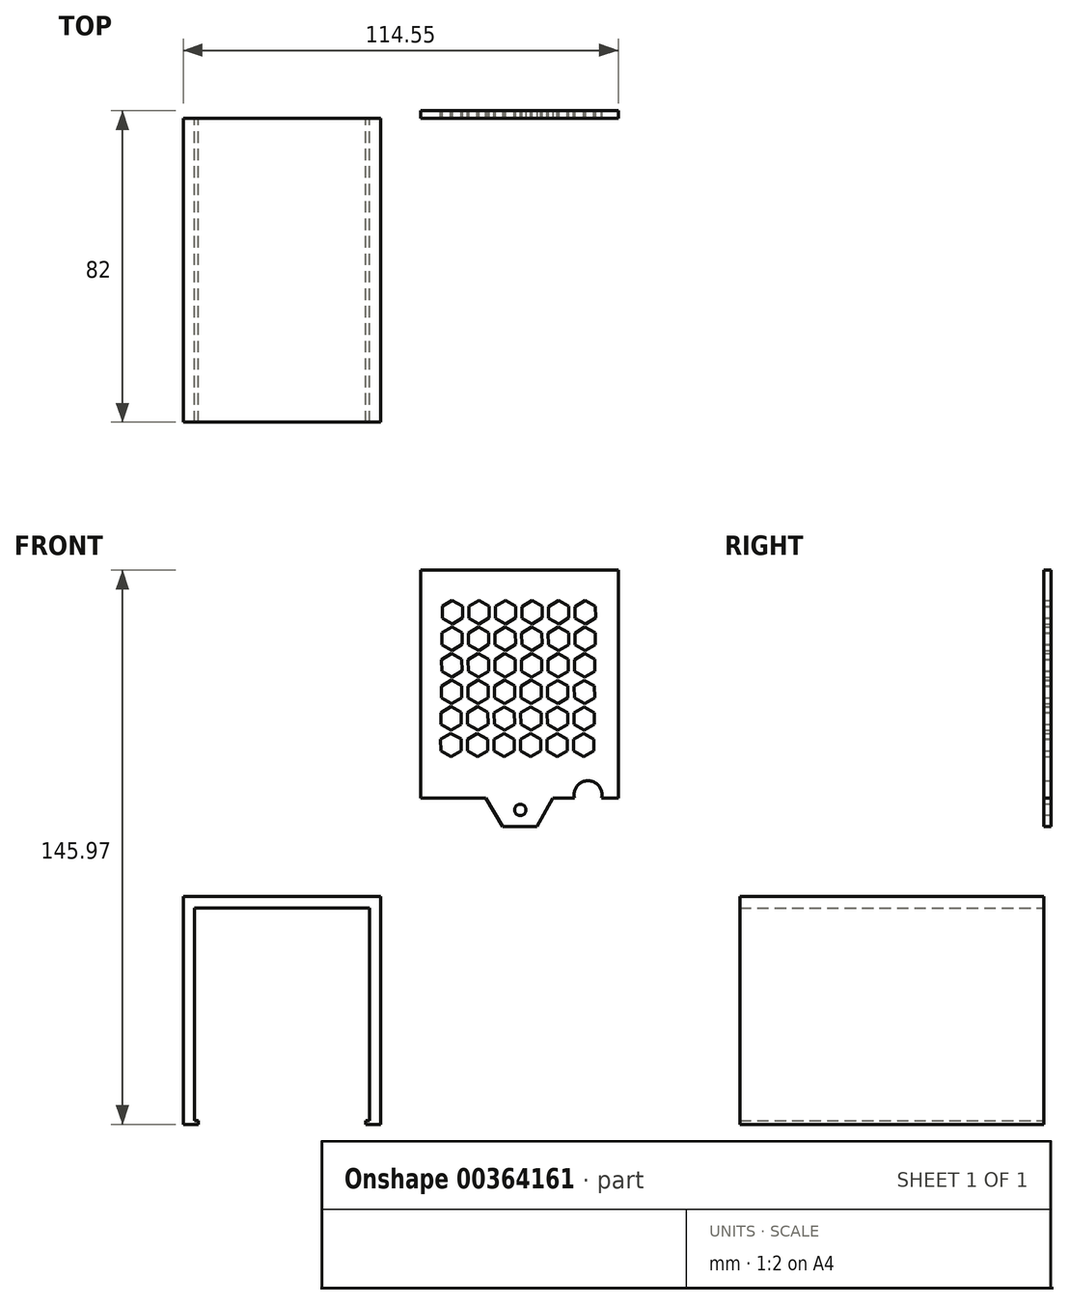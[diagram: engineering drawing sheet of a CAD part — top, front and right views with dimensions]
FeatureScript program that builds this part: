
annotation { "Feature Type Name" : "Feature", "Feature Type Description" : "" }
export const myFeature = defineFeature(function(context is Context, id is Id, definition is map)
    precondition{}
    {
        {
            var Q0;
            Q0=qCreatedBy(makeId("Front.planeOp"),FACE);
            var sketch = newSketch(context, id + "F0", { "sketchPlane" : qUnion([Q0])});
            skLineSegment(sketch, "E0", {"start": v(-25.2, -51.06) * mm, "end": v(-29.2, -51.06) * mm});
            skLineSegment(sketch, "E1", {"start": v(-29.2, -51.06) * mm, "end": v(-29.2, 8.94) * mm});
            skLineSegment(sketch, "E2", {"start": v(-29.2, 8.94) * mm, "end": v(22.8, 8.94) * mm});
            skLineSegment(sketch, "E3", {"start": v(22.8, 8.94) * mm, "end": v(22.8, -51.06) * mm});
            skLineSegment(sketch, "E4", {"start": v(22.8, -51.06) * mm, "end": v(18.8, -51.06) * mm});
            skLineSegment(sketch, "E5", {"start": v(18.8, -51.06) * mm, "end": v(18.8, -50.06) * mm});
            skLineSegment(sketch, "E6", {"start": v(18.8, -50.06) * mm, "end": v(19.8, -50.06) * mm});
            skLineSegment(sketch, "E7", {"start": v(19.8, -50.06) * mm, "end": v(19.8, 5.94) * mm});
            skLineSegment(sketch, "E8", {"start": v(19.8, 5.94) * mm, "end": v(-26.2, 5.94) * mm});
            skLineSegment(sketch, "E9", {"start": v(-26.2, 5.94) * mm, "end": v(-26.2, -50.06) * mm});
            skLineSegment(sketch, "E10", {"start": v(-26.2, -50.06) * mm, "end": v(-25.2, -50.06) * mm});
            skLineSegment(sketch, "E11", {"start": v(-25.2, -50.06) * mm, "end": v(-25.2, -51.06) * mm});
            skSolve(sketch);
        }
        {
            var Q0;
            Q0=makeQuery(id+"F0.imprint","IMPRINT",FACE,{"disambiguationData":[TD([[makeQuery(id+"F0.imprint","IMPRINT",EDGE,{"derivedFrom":sQuery(id+"F0.wireOp",EDGE,"E0")}),-1.0]])]});
            extrude(context, id + "F1", {"entities" : qUnion([Q0]), "depth" : 80 * mm});
        }
        {
            var Q0;
            Q0=qCreatedBy(makeId("Front.planeOp"),FACE);
            var sketch = newSketch(context, id + "F2", { "sketchPlane" : qUnion([Q0])});
            skLineSegment(sketch, "E12.bottom", {"start": v(85.34, 94.91) * mm, "end": v(33.34, 94.91) * mm});
            skLineSegment(sketch, "E12.top", {"start": v(85.34, 34.91) * mm, "end": v(33.34, 34.91) * mm});
            skLineSegment(sketch, "E12.left", {"start": v(85.34, 94.91) * mm, "end": v(85.34, 34.91) * mm});
            skLineSegment(sketch, "E12.right", {"start": v(33.34, 94.91) * mm, "end": v(33.34, 34.91) * mm});
            skSolve(sketch);
        }
        {
            var Q0;
            Q0=makeQuery(id+"F2.imprint","IMPRINT",FACE,{"disambiguationData":[TD([[makeQuery(id+"F2.imprint","IMPRINT",EDGE,{"derivedFrom":sQuery(id+"F2.wireOp",EDGE,"E12.bottom")}),1.0]])]});
            extrude(context, id + "F3", {"entities" : qUnion([Q0]), "oppositeDirection" : true, "depth" : 2 * mm});
        }
        {
            var Q0;
            Q0=makeQuery(id+"F3.opExtrude","CAP_FACE",FACE,{"disambiguationData":[OSD([sQuery(id+"F2.wireOp",EDGE,"E12.bottom"),sQuery(id+"F2.wireOp",EDGE,"E12.top"),sQuery(id+"F2.wireOp",EDGE,"E12.left"),sQuery(id+"F2.wireOp",EDGE,"E12.right")])],"isStart":false});
            var sketch = newSketch(context, id + "F4", { "sketchPlane" : qUnion([Q0])});
            skCircle(sketch, "E13.cCircle", {"center": v(-76.67, 83.82) * mm, "radius": 2.68 * mm, "construction": true});
            skLineSegment(sketch, "E13.0", {"start": v(-74, 82.25) * mm, "end": v(-76.7, 80.74) * mm});
            skLineSegment(sketch, "E13.1", {"start": v(-76.7, 80.74) * mm, "end": v(-79.36, 82.3) * mm});
            skLineSegment(sketch, "E13.2", {"start": v(-79.36, 82.3) * mm, "end": v(-79.33, 85.4) * mm});
            skLineSegment(sketch, "E13.3", {"start": v(-79.33, 85.4) * mm, "end": v(-76.63, 86.91) * mm});
            skLineSegment(sketch, "E13.4", {"start": v(-76.63, 86.91) * mm, "end": v(-73.98, 85.34) * mm});
            skLineSegment(sketch, "E13.5", {"start": v(-73.98, 85.34) * mm, "end": v(-74, 82.25) * mm});
            skPoint(sketch, "E13.0.midPoint", {"position": v(-75.36, 81.5) * mm});
            skLineSegment(sketch, "E14.1.0.0", {"start": v(-72.33, 85.4) * mm, "end": v(-69.63, 86.92) * mm});
            skLineSegment(sketch, "E14.1.0.1", {"start": v(-72.36, 82.32) * mm, "end": v(-72.33, 85.4) * mm});
            skLineSegment(sketch, "E14.1.0.2", {"start": v(-69.7, 80.74) * mm, "end": v(-72.36, 82.32) * mm});
            skLineSegment(sketch, "E14.1.0.3", {"start": v(-67, 82.26) * mm, "end": v(-69.7, 80.74) * mm});
            skPoint(sketch, "E14.1.0.4", {"position": v(-68.36, 81.5) * mm});
            skCircle(sketch, "E14.1.0.5", {"center": v(-69.67, 83.83) * mm, "radius": 2.68 * mm, "construction": true});
            skLineSegment(sketch, "E14.1.0.6", {"start": v(-66.98, 85.34) * mm, "end": v(-67, 82.26) * mm});
            skLineSegment(sketch, "E14.1.0.7", {"start": v(-69.63, 86.92) * mm, "end": v(-66.98, 85.34) * mm});
            skLineSegment(sketch, "E14.2.0.0", {"start": v(-65.33, 85.4) * mm, "end": v(-62.63, 86.92) * mm});
            skLineSegment(sketch, "E14.2.0.1", {"start": v(-65.36, 82.32) * mm, "end": v(-65.33, 85.4) * mm});
            skLineSegment(sketch, "E14.2.0.2", {"start": v(-62.7, 80.75) * mm, "end": v(-65.36, 82.32) * mm});
            skLineSegment(sketch, "E14.2.0.3", {"start": v(-60, 82.26) * mm, "end": v(-62.7, 80.75) * mm});
            skPoint(sketch, "E14.2.0.4", {"position": v(-61.36, 81.5) * mm});
            skCircle(sketch, "E14.2.0.5", {"center": v(-62.67, 83.84) * mm, "radius": 2.68 * mm, "construction": true});
            skLineSegment(sketch, "E14.2.0.6", {"start": v(-59.98, 85.35) * mm, "end": v(-60, 82.26) * mm});
            skLineSegment(sketch, "E14.2.0.7", {"start": v(-62.63, 86.92) * mm, "end": v(-59.98, 85.35) * mm});
            skLineSegment(sketch, "E14.3.0.0", {"start": v(-58.33, 85.42) * mm, "end": v(-55.63, 86.93) * mm});
            skLineSegment(sketch, "E14.3.0.1", {"start": v(-58.36, 82.33) * mm, "end": v(-58.33, 85.42) * mm});
            skLineSegment(sketch, "E14.3.0.2", {"start": v(-55.7, 80.75) * mm, "end": v(-58.36, 82.33) * mm});
            skLineSegment(sketch, "E14.3.0.3", {"start": v(-53, 82.27) * mm, "end": v(-55.7, 80.75) * mm});
            skPoint(sketch, "E14.3.0.4", {"position": v(-54.36, 81.5) * mm});
            skCircle(sketch, "E14.3.0.5", {"center": v(-55.67, 83.84) * mm, "radius": 2.68 * mm, "construction": true});
            skLineSegment(sketch, "E14.3.0.6", {"start": v(-52.98, 85.36) * mm, "end": v(-53, 82.27) * mm});
            skLineSegment(sketch, "E14.3.0.7", {"start": v(-55.63, 86.93) * mm, "end": v(-52.98, 85.36) * mm});
            skLineSegment(sketch, "E14.4.0.0", {"start": v(-51.33, 85.42) * mm, "end": v(-48.63, 86.94) * mm});
            skLineSegment(sketch, "E14.4.0.1", {"start": v(-51.36, 82.33) * mm, "end": v(-51.33, 85.42) * mm});
            skLineSegment(sketch, "E14.4.0.2", {"start": v(-48.7, 80.76) * mm, "end": v(-51.36, 82.33) * mm});
            skLineSegment(sketch, "E14.4.0.3", {"start": v(-46, 82.27) * mm, "end": v(-48.7, 80.76) * mm});
            skPoint(sketch, "E14.4.0.4", {"position": v(-47.36, 81.52) * mm});
            skCircle(sketch, "E14.4.0.5", {"center": v(-48.67, 83.85) * mm, "radius": 2.68 * mm, "construction": true});
            skLineSegment(sketch, "E14.4.0.6", {"start": v(-45.98, 85.36) * mm, "end": v(-46, 82.27) * mm});
            skLineSegment(sketch, "E14.4.0.7", {"start": v(-48.63, 86.94) * mm, "end": v(-45.98, 85.36) * mm});
            skLineSegment(sketch, "E14.5.0.0", {"start": v(-44.33, 85.43) * mm, "end": v(-41.63, 86.94) * mm});
            skLineSegment(sketch, "E14.5.0.1", {"start": v(-44.36, 82.34) * mm, "end": v(-44.33, 85.43) * mm});
            skLineSegment(sketch, "E14.5.0.2", {"start": v(-41.7, 80.76) * mm, "end": v(-44.36, 82.34) * mm});
            skLineSegment(sketch, "E14.5.0.3", {"start": v(-39, 82.28) * mm, "end": v(-41.7, 80.76) * mm});
            skPoint(sketch, "E14.5.0.4", {"position": v(-40.36, 81.52) * mm});
            skCircle(sketch, "E14.5.0.5", {"center": v(-41.67, 83.85) * mm, "radius": 2.68 * mm, "construction": true});
            skLineSegment(sketch, "E14.5.0.6", {"start": v(-38.98, 85.37) * mm, "end": v(-39, 82.28) * mm});
            skLineSegment(sketch, "E14.5.0.7", {"start": v(-41.63, 86.94) * mm, "end": v(-38.98, 85.37) * mm});
            skLineSegment(sketch, "E14.direction1", {"start": v(-79.36, 82.3) * mm, "end": v(-72.36, 82.32) * mm, "construction": true});
            skPoint(sketch, "E15.1.0.0", {"position": v(-75.28, 74.5) * mm});
            skPoint(sketch, "E15.1.0.1", {"position": v(-68.28, 74.5) * mm});
            skPoint(sketch, "E15.1.0.2", {"position": v(-61.28, 74.5) * mm});
            skPoint(sketch, "E15.1.0.3", {"position": v(-54.28, 74.51) * mm});
            skPoint(sketch, "E15.1.0.4", {"position": v(-47.28, 74.52) * mm});
            skPoint(sketch, "E15.1.0.5", {"position": v(-40.28, 74.52) * mm});
            skLineSegment(sketch, "E15.1.0.7", {"start": v(-38.93, 75.28) * mm, "end": v(-41.62, 73.76) * mm});
            skLineSegment(sketch, "E15.1.0.8", {"start": v(-58.28, 75.33) * mm, "end": v(-58.24, 78.42) * mm});
            skLineSegment(sketch, "E15.1.0.9", {"start": v(-55.62, 73.75) * mm, "end": v(-58.28, 75.33) * mm});
            skCircle(sketch, "E15.1.0.10", {"center": v(-41.59, 76.85) * mm, "radius": 2.68 * mm, "construction": true});
            skLineSegment(sketch, "E15.1.0.11", {"start": v(-52.93, 75.27) * mm, "end": v(-55.62, 73.75) * mm});
            skLineSegment(sketch, "E15.1.0.12", {"start": v(-38.9, 78.37) * mm, "end": v(-38.93, 75.28) * mm});
            skCircle(sketch, "E15.1.0.13", {"center": v(-55.59, 76.84) * mm, "radius": 2.68 * mm, "construction": true});
            skLineSegment(sketch, "E15.1.0.14", {"start": v(-52.9, 78.36) * mm, "end": v(-52.93, 75.27) * mm});
            skLineSegment(sketch, "E15.1.0.16", {"start": v(-55.55, 79.93) * mm, "end": v(-52.9, 78.36) * mm});
            skLineSegment(sketch, "E15.1.0.20", {"start": v(-51.28, 75.33) * mm, "end": v(-51.24, 78.42) * mm});
            skLineSegment(sketch, "E15.1.0.22", {"start": v(-48.62, 73.76) * mm, "end": v(-51.28, 75.33) * mm});
            skLineSegment(sketch, "E15.1.0.24", {"start": v(-45.93, 75.27) * mm, "end": v(-48.62, 73.76) * mm});
            skCircle(sketch, "E15.1.0.26", {"center": v(-48.59, 76.85) * mm, "radius": 2.68 * mm, "construction": true});
            skLineSegment(sketch, "E15.1.0.27", {"start": v(-62.62, 73.75) * mm, "end": v(-65.28, 75.32) * mm});
            skLineSegment(sketch, "E15.1.0.28", {"start": v(-79.28, 75.31) * mm, "end": v(-72.28, 75.32) * mm, "construction": true});
            skLineSegment(sketch, "E15.1.0.29", {"start": v(-45.9, 78.36) * mm, "end": v(-45.93, 75.27) * mm});
            skLineSegment(sketch, "E15.1.0.30", {"start": v(-59.93, 75.26) * mm, "end": v(-62.62, 73.75) * mm});
            skLineSegment(sketch, "E15.1.0.31", {"start": v(-48.55, 79.94) * mm, "end": v(-45.9, 78.36) * mm});
            skCircle(sketch, "E15.1.0.32", {"center": v(-62.59, 76.84) * mm, "radius": 2.68 * mm, "construction": true});
            skLineSegment(sketch, "E15.1.0.33", {"start": v(-44.24, 78.43) * mm, "end": v(-41.55, 79.94) * mm});
            skLineSegment(sketch, "E15.1.0.34", {"start": v(-59.9, 78.35) * mm, "end": v(-59.93, 75.26) * mm});
            skLineSegment(sketch, "E15.1.0.35", {"start": v(-69.55, 79.92) * mm, "end": v(-66.9, 78.35) * mm});
            skLineSegment(sketch, "E15.1.0.36", {"start": v(-65.24, 78.41) * mm, "end": v(-62.55, 79.93) * mm});
            skLineSegment(sketch, "E15.1.0.37", {"start": v(-65.28, 75.32) * mm, "end": v(-65.24, 78.41) * mm});
            skCircle(sketch, "E15.1.0.38", {"center": v(-76.59, 76.82) * mm, "radius": 2.68 * mm, "construction": true});
            skLineSegment(sketch, "E15.1.0.39", {"start": v(-73.93, 75.25) * mm, "end": v(-76.62, 73.74) * mm});
            skLineSegment(sketch, "E15.1.0.40", {"start": v(-76.62, 73.74) * mm, "end": v(-79.28, 75.31) * mm});
            skLineSegment(sketch, "E15.1.0.41", {"start": v(-79.28, 75.31) * mm, "end": v(-79.24, 78.4) * mm});
            skLineSegment(sketch, "E15.1.0.42", {"start": v(-76.55, 79.91) * mm, "end": v(-73.9, 78.34) * mm});
            skLineSegment(sketch, "E15.1.0.43", {"start": v(-72.24, 78.4) * mm, "end": v(-69.55, 79.92) * mm});
            skLineSegment(sketch, "E15.1.0.44", {"start": v(-72.28, 75.32) * mm, "end": v(-72.24, 78.4) * mm});
            skLineSegment(sketch, "E15.1.0.45", {"start": v(-69.62, 73.74) * mm, "end": v(-72.28, 75.32) * mm});
            skLineSegment(sketch, "E15.1.0.46", {"start": v(-66.93, 75.26) * mm, "end": v(-69.62, 73.74) * mm});
            skLineSegment(sketch, "E15.1.0.47", {"start": v(-44.28, 75.34) * mm, "end": v(-44.24, 78.43) * mm});
            skLineSegment(sketch, "E15.1.0.48", {"start": v(-62.55, 79.93) * mm, "end": v(-59.9, 78.35) * mm});
            skCircle(sketch, "E15.1.0.49", {"center": v(-69.59, 76.83) * mm, "radius": 2.68 * mm, "construction": true});
            skLineSegment(sketch, "E15.1.0.50", {"start": v(-66.9, 78.35) * mm, "end": v(-66.93, 75.26) * mm});
            skLineSegment(sketch, "E15.1.0.51", {"start": v(-41.62, 73.76) * mm, "end": v(-44.28, 75.34) * mm});
            skLineSegment(sketch, "E15.1.0.52", {"start": v(-58.24, 78.42) * mm, "end": v(-55.55, 79.93) * mm});
            skLineSegment(sketch, "E15.1.0.53", {"start": v(-41.55, 79.94) * mm, "end": v(-38.9, 78.37) * mm});
            skLineSegment(sketch, "E15.1.0.54", {"start": v(-51.24, 78.42) * mm, "end": v(-48.55, 79.94) * mm});
            skLineSegment(sketch, "E15.1.0.55", {"start": v(-79.24, 78.4) * mm, "end": v(-76.55, 79.91) * mm});
            skLineSegment(sketch, "E15.1.0.56", {"start": v(-73.9, 78.34) * mm, "end": v(-73.93, 75.25) * mm});
            skPoint(sketch, "E15.2.0.0", {"position": v(-75.2, 67.5) * mm});
            skPoint(sketch, "E15.2.0.1", {"position": v(-68.2, 67.5) * mm});
            skPoint(sketch, "E15.2.0.2", {"position": v(-61.2, 67.5) * mm});
            skPoint(sketch, "E15.2.0.3", {"position": v(-54.2, 67.51) * mm});
            skPoint(sketch, "E15.2.0.4", {"position": v(-47.2, 67.52) * mm});
            skPoint(sketch, "E15.2.0.5", {"position": v(-40.2, 67.52) * mm});
            skLineSegment(sketch, "E15.2.0.7", {"start": v(-38.85, 68.28) * mm, "end": v(-41.54, 66.76) * mm});
            skLineSegment(sketch, "E15.2.0.8", {"start": v(-58.2, 68.33) * mm, "end": v(-58.16, 71.42) * mm});
            skLineSegment(sketch, "E15.2.0.9", {"start": v(-55.54, 66.75) * mm, "end": v(-58.2, 68.33) * mm});
            skCircle(sketch, "E15.2.0.10", {"center": v(-41.5, 69.85) * mm, "radius": 2.68 * mm, "construction": true});
            skLineSegment(sketch, "E15.2.0.11", {"start": v(-52.85, 68.27) * mm, "end": v(-55.54, 66.75) * mm});
            skLineSegment(sketch, "E15.2.0.12", {"start": v(-38.81, 71.37) * mm, "end": v(-38.85, 68.28) * mm});
            skCircle(sketch, "E15.2.0.13", {"center": v(-55.5, 69.84) * mm, "radius": 2.68 * mm, "construction": true});
            skLineSegment(sketch, "E15.2.0.14", {"start": v(-52.81, 71.36) * mm, "end": v(-52.85, 68.27) * mm});
            skLineSegment(sketch, "E15.2.0.16", {"start": v(-55.47, 72.93) * mm, "end": v(-52.81, 71.36) * mm});
            skLineSegment(sketch, "E15.2.0.20", {"start": v(-51.2, 68.33) * mm, "end": v(-51.16, 71.42) * mm});
            skLineSegment(sketch, "E15.2.0.22", {"start": v(-48.54, 66.76) * mm, "end": v(-51.2, 68.33) * mm});
            skLineSegment(sketch, "E15.2.0.24", {"start": v(-45.85, 68.27) * mm, "end": v(-48.54, 66.76) * mm});
            skCircle(sketch, "E15.2.0.26", {"center": v(-48.5, 69.85) * mm, "radius": 2.68 * mm, "construction": true});
            skLineSegment(sketch, "E15.2.0.27", {"start": v(-62.54, 66.75) * mm, "end": v(-65.2, 68.32) * mm});
            skLineSegment(sketch, "E15.2.0.28", {"start": v(-79.2, 68.31) * mm, "end": v(-72.2, 68.32) * mm, "construction": true});
            skLineSegment(sketch, "E15.2.0.29", {"start": v(-45.81, 71.36) * mm, "end": v(-45.85, 68.27) * mm});
            skLineSegment(sketch, "E15.2.0.30", {"start": v(-59.85, 68.26) * mm, "end": v(-62.54, 66.75) * mm});
            skLineSegment(sketch, "E15.2.0.31", {"start": v(-48.47, 72.94) * mm, "end": v(-45.81, 71.36) * mm});
            skCircle(sketch, "E15.2.0.32", {"center": v(-62.5, 69.84) * mm, "radius": 2.68 * mm, "construction": true});
            skLineSegment(sketch, "E15.2.0.33", {"start": v(-44.16, 71.43) * mm, "end": v(-41.47, 72.94) * mm});
            skLineSegment(sketch, "E15.2.0.34", {"start": v(-59.81, 71.35) * mm, "end": v(-59.85, 68.26) * mm});
            skLineSegment(sketch, "E15.2.0.35", {"start": v(-69.47, 72.92) * mm, "end": v(-66.81, 71.35) * mm});
            skLineSegment(sketch, "E15.2.0.36", {"start": v(-65.16, 71.41) * mm, "end": v(-62.47, 72.93) * mm});
            skLineSegment(sketch, "E15.2.0.37", {"start": v(-65.2, 68.32) * mm, "end": v(-65.16, 71.41) * mm});
            skCircle(sketch, "E15.2.0.38", {"center": v(-76.5, 69.83) * mm, "radius": 2.68 * mm, "construction": true});
            skLineSegment(sketch, "E15.2.0.39", {"start": v(-73.85, 68.25) * mm, "end": v(-76.54, 66.74) * mm});
            skLineSegment(sketch, "E15.2.0.40", {"start": v(-76.54, 66.74) * mm, "end": v(-79.2, 68.31) * mm});
            skLineSegment(sketch, "E15.2.0.41", {"start": v(-79.2, 68.31) * mm, "end": v(-79.16, 71.4) * mm});
            skLineSegment(sketch, "E15.2.0.42", {"start": v(-76.47, 72.91) * mm, "end": v(-73.81, 71.34) * mm});
            skLineSegment(sketch, "E15.2.0.43", {"start": v(-72.16, 71.4) * mm, "end": v(-69.47, 72.92) * mm});
            skLineSegment(sketch, "E15.2.0.44", {"start": v(-72.2, 68.32) * mm, "end": v(-72.16, 71.4) * mm});
            skLineSegment(sketch, "E15.2.0.45", {"start": v(-69.54, 66.74) * mm, "end": v(-72.2, 68.32) * mm});
            skLineSegment(sketch, "E15.2.0.46", {"start": v(-66.85, 68.26) * mm, "end": v(-69.54, 66.74) * mm});
            skLineSegment(sketch, "E15.2.0.47", {"start": v(-44.2, 68.34) * mm, "end": v(-44.16, 71.43) * mm});
            skLineSegment(sketch, "E15.2.0.48", {"start": v(-62.47, 72.93) * mm, "end": v(-59.81, 71.35) * mm});
            skCircle(sketch, "E15.2.0.49", {"center": v(-69.5, 69.83) * mm, "radius": 2.68 * mm, "construction": true});
            skLineSegment(sketch, "E15.2.0.50", {"start": v(-66.81, 71.35) * mm, "end": v(-66.85, 68.26) * mm});
            skLineSegment(sketch, "E15.2.0.51", {"start": v(-41.54, 66.76) * mm, "end": v(-44.2, 68.34) * mm});
            skLineSegment(sketch, "E15.2.0.52", {"start": v(-58.16, 71.42) * mm, "end": v(-55.47, 72.93) * mm});
            skLineSegment(sketch, "E15.2.0.53", {"start": v(-41.47, 72.94) * mm, "end": v(-38.81, 71.37) * mm});
            skLineSegment(sketch, "E15.2.0.54", {"start": v(-51.16, 71.42) * mm, "end": v(-48.47, 72.94) * mm});
            skLineSegment(sketch, "E15.2.0.55", {"start": v(-79.16, 71.4) * mm, "end": v(-76.47, 72.91) * mm});
            skLineSegment(sketch, "E15.2.0.56", {"start": v(-73.81, 71.34) * mm, "end": v(-73.85, 68.25) * mm});
            skPoint(sketch, "E15.3.0.0", {"position": v(-75.11, 60.5) * mm});
            skPoint(sketch, "E15.3.0.1", {"position": v(-68.11, 60.5) * mm});
            skPoint(sketch, "E15.3.0.2", {"position": v(-61.11, 60.5) * mm});
            skPoint(sketch, "E15.3.0.3", {"position": v(-54.11, 60.51) * mm});
            skPoint(sketch, "E15.3.0.4", {"position": v(-47.11, 60.52) * mm});
            skPoint(sketch, "E15.3.0.5", {"position": v(-40.11, 60.52) * mm});
            skLineSegment(sketch, "E15.3.0.7", {"start": v(-38.77, 61.28) * mm, "end": v(-41.46, 59.77) * mm});
            skLineSegment(sketch, "E15.3.0.8", {"start": v(-58.12, 61.33) * mm, "end": v(-58.08, 64.42) * mm});
            skLineSegment(sketch, "E15.3.0.9", {"start": v(-55.46, 59.75) * mm, "end": v(-58.12, 61.33) * mm});
            skCircle(sketch, "E15.3.0.10", {"center": v(-41.43, 62.85) * mm, "radius": 2.68 * mm, "construction": true});
            skLineSegment(sketch, "E15.3.0.11", {"start": v(-52.77, 61.27) * mm, "end": v(-55.46, 59.75) * mm});
            skLineSegment(sketch, "E15.3.0.12", {"start": v(-38.73, 64.37) * mm, "end": v(-38.77, 61.28) * mm});
            skCircle(sketch, "E15.3.0.13", {"center": v(-55.43, 62.84) * mm, "radius": 2.68 * mm, "construction": true});
            skLineSegment(sketch, "E15.3.0.14", {"start": v(-52.73, 64.36) * mm, "end": v(-52.77, 61.27) * mm});
            skLineSegment(sketch, "E15.3.0.16", {"start": v(-55.4, 65.93) * mm, "end": v(-52.73, 64.36) * mm});
            skLineSegment(sketch, "E15.3.0.20", {"start": v(-51.12, 61.33) * mm, "end": v(-51.08, 64.42) * mm});
            skLineSegment(sketch, "E15.3.0.22", {"start": v(-48.46, 59.76) * mm, "end": v(-51.12, 61.33) * mm});
            skLineSegment(sketch, "E15.3.0.24", {"start": v(-45.77, 61.27) * mm, "end": v(-48.46, 59.76) * mm});
            skCircle(sketch, "E15.3.0.26", {"center": v(-48.43, 62.85) * mm, "radius": 2.68 * mm, "construction": true});
            skLineSegment(sketch, "E15.3.0.27", {"start": v(-62.46, 59.75) * mm, "end": v(-65.12, 61.32) * mm});
            skLineSegment(sketch, "E15.3.0.28", {"start": v(-79.12, 61.31) * mm, "end": v(-72.12, 61.32) * mm, "construction": true});
            skLineSegment(sketch, "E15.3.0.29", {"start": v(-45.73, 64.36) * mm, "end": v(-45.77, 61.27) * mm});
            skLineSegment(sketch, "E15.3.0.30", {"start": v(-59.77, 61.26) * mm, "end": v(-62.46, 59.75) * mm});
            skLineSegment(sketch, "E15.3.0.31", {"start": v(-48.4, 65.94) * mm, "end": v(-45.73, 64.36) * mm});
            skCircle(sketch, "E15.3.0.32", {"center": v(-62.43, 62.84) * mm, "radius": 2.68 * mm, "construction": true});
            skLineSegment(sketch, "E15.3.0.33", {"start": v(-44.08, 64.43) * mm, "end": v(-41.4, 65.94) * mm});
            skLineSegment(sketch, "E15.3.0.34", {"start": v(-59.73, 64.35) * mm, "end": v(-59.77, 61.26) * mm});
            skLineSegment(sketch, "E15.3.0.35", {"start": v(-69.4, 65.92) * mm, "end": v(-66.73, 64.35) * mm});
            skLineSegment(sketch, "E15.3.0.36", {"start": v(-65.08, 64.41) * mm, "end": v(-62.4, 65.93) * mm});
            skLineSegment(sketch, "E15.3.0.37", {"start": v(-65.12, 61.32) * mm, "end": v(-65.08, 64.41) * mm});
            skCircle(sketch, "E15.3.0.38", {"center": v(-76.43, 62.83) * mm, "radius": 2.68 * mm, "construction": true});
            skLineSegment(sketch, "E15.3.0.39", {"start": v(-73.77, 61.25) * mm, "end": v(-76.46, 59.74) * mm});
            skLineSegment(sketch, "E15.3.0.40", {"start": v(-76.46, 59.74) * mm, "end": v(-79.12, 61.31) * mm});
            skLineSegment(sketch, "E15.3.0.41", {"start": v(-79.12, 61.31) * mm, "end": v(-79.08, 64.4) * mm});
            skLineSegment(sketch, "E15.3.0.42", {"start": v(-76.4, 65.91) * mm, "end": v(-73.73, 64.34) * mm});
            skLineSegment(sketch, "E15.3.0.43", {"start": v(-72.08, 64.4) * mm, "end": v(-69.4, 65.92) * mm});
            skLineSegment(sketch, "E15.3.0.44", {"start": v(-72.12, 61.32) * mm, "end": v(-72.08, 64.4) * mm});
            skLineSegment(sketch, "E15.3.0.45", {"start": v(-69.46, 59.74) * mm, "end": v(-72.12, 61.32) * mm});
            skLineSegment(sketch, "E15.3.0.46", {"start": v(-66.77, 61.26) * mm, "end": v(-69.46, 59.74) * mm});
            skLineSegment(sketch, "E15.3.0.47", {"start": v(-44.12, 61.34) * mm, "end": v(-44.08, 64.43) * mm});
            skLineSegment(sketch, "E15.3.0.48", {"start": v(-62.4, 65.93) * mm, "end": v(-59.73, 64.35) * mm});
            skCircle(sketch, "E15.3.0.49", {"center": v(-69.43, 62.83) * mm, "radius": 2.68 * mm, "construction": true});
            skLineSegment(sketch, "E15.3.0.50", {"start": v(-66.73, 64.35) * mm, "end": v(-66.77, 61.26) * mm});
            skLineSegment(sketch, "E15.3.0.51", {"start": v(-41.46, 59.77) * mm, "end": v(-44.12, 61.34) * mm});
            skLineSegment(sketch, "E15.3.0.52", {"start": v(-58.08, 64.42) * mm, "end": v(-55.4, 65.93) * mm});
            skLineSegment(sketch, "E15.3.0.53", {"start": v(-41.4, 65.94) * mm, "end": v(-38.73, 64.37) * mm});
            skLineSegment(sketch, "E15.3.0.54", {"start": v(-51.08, 64.42) * mm, "end": v(-48.4, 65.94) * mm});
            skLineSegment(sketch, "E15.3.0.55", {"start": v(-79.08, 64.4) * mm, "end": v(-76.4, 65.91) * mm});
            skLineSegment(sketch, "E15.3.0.56", {"start": v(-73.73, 64.34) * mm, "end": v(-73.77, 61.25) * mm});
            skPoint(sketch, "E15.4.0.0", {"position": v(-75.03, 53.5) * mm});
            skPoint(sketch, "E15.4.0.1", {"position": v(-68.03, 53.5) * mm});
            skPoint(sketch, "E15.4.0.2", {"position": v(-61.03, 53.5) * mm});
            skPoint(sketch, "E15.4.0.3", {"position": v(-54.03, 53.51) * mm});
            skPoint(sketch, "E15.4.0.4", {"position": v(-47.03, 53.52) * mm});
            skPoint(sketch, "E15.4.0.5", {"position": v(-40.03, 53.52) * mm});
            skLineSegment(sketch, "E15.4.0.7", {"start": v(-38.69, 54.28) * mm, "end": v(-41.38, 52.77) * mm});
            skLineSegment(sketch, "E15.4.0.8", {"start": v(-58.04, 54.33) * mm, "end": v(-58, 57.42) * mm});
            skLineSegment(sketch, "E15.4.0.9", {"start": v(-55.38, 52.75) * mm, "end": v(-58.04, 54.33) * mm});
            skCircle(sketch, "E15.4.0.10", {"center": v(-41.34, 55.85) * mm, "radius": 2.68 * mm, "construction": true});
            skLineSegment(sketch, "E15.4.0.11", {"start": v(-52.69, 54.27) * mm, "end": v(-55.38, 52.75) * mm});
            skLineSegment(sketch, "E15.4.0.12", {"start": v(-38.65, 57.37) * mm, "end": v(-38.69, 54.28) * mm});
            skCircle(sketch, "E15.4.0.13", {"center": v(-55.34, 55.84) * mm, "radius": 2.68 * mm, "construction": true});
            skLineSegment(sketch, "E15.4.0.14", {"start": v(-52.65, 57.36) * mm, "end": v(-52.69, 54.27) * mm});
            skLineSegment(sketch, "E15.4.0.16", {"start": v(-55.31, 58.93) * mm, "end": v(-52.65, 57.36) * mm});
            skLineSegment(sketch, "E15.4.0.20", {"start": v(-51.04, 54.33) * mm, "end": v(-51, 57.42) * mm});
            skLineSegment(sketch, "E15.4.0.22", {"start": v(-48.38, 52.76) * mm, "end": v(-51.04, 54.33) * mm});
            skLineSegment(sketch, "E15.4.0.24", {"start": v(-45.69, 54.27) * mm, "end": v(-48.38, 52.76) * mm});
            skCircle(sketch, "E15.4.0.26", {"center": v(-48.34, 55.85) * mm, "radius": 2.68 * mm, "construction": true});
            skLineSegment(sketch, "E15.4.0.27", {"start": v(-62.38, 52.75) * mm, "end": v(-65.04, 54.32) * mm});
            skLineSegment(sketch, "E15.4.0.28", {"start": v(-79.04, 54.31) * mm, "end": v(-72.04, 54.32) * mm, "construction": true});
            skLineSegment(sketch, "E15.4.0.29", {"start": v(-45.65, 57.36) * mm, "end": v(-45.69, 54.27) * mm});
            skLineSegment(sketch, "E15.4.0.30", {"start": v(-59.69, 54.26) * mm, "end": v(-62.38, 52.75) * mm});
            skLineSegment(sketch, "E15.4.0.31", {"start": v(-48.31, 58.94) * mm, "end": v(-45.65, 57.36) * mm});
            skCircle(sketch, "E15.4.0.32", {"center": v(-62.34, 55.84) * mm, "radius": 2.68 * mm, "construction": true});
            skLineSegment(sketch, "E15.4.0.33", {"start": v(-44, 57.43) * mm, "end": v(-41.31, 58.94) * mm});
            skLineSegment(sketch, "E15.4.0.34", {"start": v(-59.65, 57.35) * mm, "end": v(-59.69, 54.26) * mm});
            skLineSegment(sketch, "E15.4.0.35", {"start": v(-69.31, 58.92) * mm, "end": v(-66.65, 57.35) * mm});
            skLineSegment(sketch, "E15.4.0.36", {"start": v(-65, 57.41) * mm, "end": v(-62.31, 58.93) * mm});
            skLineSegment(sketch, "E15.4.0.37", {"start": v(-65.04, 54.32) * mm, "end": v(-65, 57.41) * mm});
            skCircle(sketch, "E15.4.0.38", {"center": v(-76.34, 55.83) * mm, "radius": 2.68 * mm, "construction": true});
            skLineSegment(sketch, "E15.4.0.39", {"start": v(-73.69, 54.25) * mm, "end": v(-76.38, 52.74) * mm});
            skLineSegment(sketch, "E15.4.0.40", {"start": v(-76.38, 52.74) * mm, "end": v(-79.04, 54.31) * mm});
            skLineSegment(sketch, "E15.4.0.41", {"start": v(-79.04, 54.31) * mm, "end": v(-79, 57.4) * mm});
            skLineSegment(sketch, "E15.4.0.42", {"start": v(-76.31, 58.92) * mm, "end": v(-73.65, 57.34) * mm});
            skLineSegment(sketch, "E15.4.0.43", {"start": v(-72, 57.4) * mm, "end": v(-69.31, 58.92) * mm});
            skLineSegment(sketch, "E15.4.0.44", {"start": v(-72.04, 54.32) * mm, "end": v(-72, 57.4) * mm});
            skLineSegment(sketch, "E15.4.0.45", {"start": v(-69.38, 52.74) * mm, "end": v(-72.04, 54.32) * mm});
            skLineSegment(sketch, "E15.4.0.46", {"start": v(-66.69, 54.26) * mm, "end": v(-69.38, 52.74) * mm});
            skLineSegment(sketch, "E15.4.0.47", {"start": v(-44.04, 54.34) * mm, "end": v(-44, 57.43) * mm});
            skLineSegment(sketch, "E15.4.0.48", {"start": v(-62.31, 58.93) * mm, "end": v(-59.65, 57.35) * mm});
            skCircle(sketch, "E15.4.0.49", {"center": v(-69.34, 55.83) * mm, "radius": 2.68 * mm, "construction": true});
            skLineSegment(sketch, "E15.4.0.50", {"start": v(-66.65, 57.35) * mm, "end": v(-66.69, 54.26) * mm});
            skLineSegment(sketch, "E15.4.0.51", {"start": v(-41.38, 52.77) * mm, "end": v(-44.04, 54.34) * mm});
            skLineSegment(sketch, "E15.4.0.52", {"start": v(-58, 57.42) * mm, "end": v(-55.31, 58.93) * mm});
            skLineSegment(sketch, "E15.4.0.53", {"start": v(-41.31, 58.94) * mm, "end": v(-38.65, 57.37) * mm});
            skLineSegment(sketch, "E15.4.0.54", {"start": v(-51, 57.42) * mm, "end": v(-48.31, 58.94) * mm});
            skLineSegment(sketch, "E15.4.0.55", {"start": v(-79, 57.4) * mm, "end": v(-76.31, 58.92) * mm});
            skLineSegment(sketch, "E15.4.0.56", {"start": v(-73.65, 57.34) * mm, "end": v(-73.69, 54.25) * mm});
            skPoint(sketch, "E15.5.0.0", {"position": v(-74.95, 46.5) * mm});
            skPoint(sketch, "E15.5.0.1", {"position": v(-67.95, 46.5) * mm});
            skPoint(sketch, "E15.5.0.2", {"position": v(-60.95, 46.5) * mm});
            skPoint(sketch, "E15.5.0.3", {"position": v(-53.95, 46.51) * mm});
            skPoint(sketch, "E15.5.0.4", {"position": v(-46.95, 46.52) * mm});
            skPoint(sketch, "E15.5.0.5", {"position": v(-39.95, 46.52) * mm});
            skLineSegment(sketch, "E15.5.0.7", {"start": v(-38.6, 47.28) * mm, "end": v(-41.3, 45.77) * mm});
            skLineSegment(sketch, "E15.5.0.8", {"start": v(-57.96, 47.33) * mm, "end": v(-57.92, 50.42) * mm});
            skLineSegment(sketch, "E15.5.0.9", {"start": v(-55.3, 45.75) * mm, "end": v(-57.96, 47.33) * mm});
            skCircle(sketch, "E15.5.0.10", {"center": v(-41.26, 48.86) * mm, "radius": 2.68 * mm, "construction": true});
            skLineSegment(sketch, "E15.5.0.11", {"start": v(-52.6, 47.27) * mm, "end": v(-55.3, 45.75) * mm});
            skLineSegment(sketch, "E15.5.0.12", {"start": v(-38.57, 50.37) * mm, "end": v(-38.6, 47.28) * mm});
            skCircle(sketch, "E15.5.0.13", {"center": v(-55.26, 48.84) * mm, "radius": 2.68 * mm, "construction": true});
            skLineSegment(sketch, "E15.5.0.14", {"start": v(-52.57, 50.36) * mm, "end": v(-52.6, 47.27) * mm});
            skLineSegment(sketch, "E15.5.0.16", {"start": v(-55.23, 51.93) * mm, "end": v(-52.57, 50.36) * mm});
            skLineSegment(sketch, "E15.5.0.20", {"start": v(-50.96, 47.33) * mm, "end": v(-50.92, 50.42) * mm});
            skLineSegment(sketch, "E15.5.0.22", {"start": v(-48.3, 45.76) * mm, "end": v(-50.96, 47.33) * mm});
            skLineSegment(sketch, "E15.5.0.24", {"start": v(-45.6, 47.28) * mm, "end": v(-48.3, 45.76) * mm});
            skCircle(sketch, "E15.5.0.26", {"center": v(-48.26, 48.85) * mm, "radius": 2.68 * mm, "construction": true});
            skLineSegment(sketch, "E15.5.0.27", {"start": v(-62.3, 45.75) * mm, "end": v(-64.96, 47.32) * mm});
            skLineSegment(sketch, "E15.5.0.28", {"start": v(-78.96, 47.31) * mm, "end": v(-71.96, 47.32) * mm, "construction": true});
            skLineSegment(sketch, "E15.5.0.29", {"start": v(-45.57, 50.36) * mm, "end": v(-45.6, 47.28) * mm});
            skLineSegment(sketch, "E15.5.0.30", {"start": v(-59.6, 47.26) * mm, "end": v(-62.3, 45.75) * mm});
            skLineSegment(sketch, "E15.5.0.31", {"start": v(-48.23, 51.94) * mm, "end": v(-45.57, 50.36) * mm});
            skCircle(sketch, "E15.5.0.32", {"center": v(-62.26, 48.84) * mm, "radius": 2.68 * mm, "construction": true});
            skLineSegment(sketch, "E15.5.0.33", {"start": v(-43.92, 50.43) * mm, "end": v(-41.23, 51.94) * mm});
            skLineSegment(sketch, "E15.5.0.34", {"start": v(-59.57, 50.35) * mm, "end": v(-59.6, 47.26) * mm});
            skLineSegment(sketch, "E15.5.0.35", {"start": v(-69.23, 51.92) * mm, "end": v(-66.57, 50.35) * mm});
            skLineSegment(sketch, "E15.5.0.36", {"start": v(-64.92, 50.41) * mm, "end": v(-62.23, 51.93) * mm});
            skLineSegment(sketch, "E15.5.0.37", {"start": v(-64.96, 47.32) * mm, "end": v(-64.92, 50.41) * mm});
            skCircle(sketch, "E15.5.0.38", {"center": v(-76.26, 48.83) * mm, "radius": 2.68 * mm, "construction": true});
            skLineSegment(sketch, "E15.5.0.39", {"start": v(-73.6, 47.25) * mm, "end": v(-76.3, 45.74) * mm});
            skLineSegment(sketch, "E15.5.0.40", {"start": v(-76.3, 45.74) * mm, "end": v(-78.96, 47.31) * mm});
            skLineSegment(sketch, "E15.5.0.41", {"start": v(-78.96, 47.31) * mm, "end": v(-78.92, 50.4) * mm});
            skLineSegment(sketch, "E15.5.0.42", {"start": v(-76.23, 51.92) * mm, "end": v(-73.57, 50.34) * mm});
            skLineSegment(sketch, "E15.5.0.43", {"start": v(-71.92, 50.4) * mm, "end": v(-69.23, 51.92) * mm});
            skLineSegment(sketch, "E15.5.0.44", {"start": v(-71.96, 47.32) * mm, "end": v(-71.92, 50.4) * mm});
            skLineSegment(sketch, "E15.5.0.45", {"start": v(-69.3, 45.74) * mm, "end": v(-71.96, 47.32) * mm});
            skLineSegment(sketch, "E15.5.0.46", {"start": v(-66.6, 47.26) * mm, "end": v(-69.3, 45.74) * mm});
            skLineSegment(sketch, "E15.5.0.47", {"start": v(-43.96, 47.34) * mm, "end": v(-43.92, 50.43) * mm});
            skLineSegment(sketch, "E15.5.0.48", {"start": v(-62.23, 51.93) * mm, "end": v(-59.57, 50.35) * mm});
            skCircle(sketch, "E15.5.0.49", {"center": v(-69.26, 48.83) * mm, "radius": 2.68 * mm, "construction": true});
            skLineSegment(sketch, "E15.5.0.50", {"start": v(-66.57, 50.35) * mm, "end": v(-66.6, 47.26) * mm});
            skLineSegment(sketch, "E15.5.0.51", {"start": v(-41.3, 45.77) * mm, "end": v(-43.96, 47.34) * mm});
            skLineSegment(sketch, "E15.5.0.52", {"start": v(-57.92, 50.42) * mm, "end": v(-55.23, 51.93) * mm});
            skLineSegment(sketch, "E15.5.0.53", {"start": v(-41.23, 51.94) * mm, "end": v(-38.57, 50.37) * mm});
            skLineSegment(sketch, "E15.5.0.54", {"start": v(-50.92, 50.42) * mm, "end": v(-48.23, 51.94) * mm});
            skLineSegment(sketch, "E15.5.0.55", {"start": v(-78.92, 50.4) * mm, "end": v(-76.23, 51.92) * mm});
            skLineSegment(sketch, "E15.5.0.56", {"start": v(-73.57, 50.34) * mm, "end": v(-73.6, 47.25) * mm});
            skLineSegment(sketch, "E15.direction1", {"start": v(-79.36, 82.3) * mm, "end": v(-79.28, 75.31) * mm, "construction": true});
            skSolve(sketch);
        }
        {
            var Q0;
            Q0 = qSketchRegion(id + "F4", true);
            extrude(context, id + "F5", {"entities" : qUnion([Q0]), "operationType" : NewBodyOperationType.REMOVE, "oppositeDirection" : true, "depth" : 2 * mm});
        }
        {
            var Q0;
            Q0=qCreatedBy(makeId("Front.planeOp"),FACE);
            var sketch = newSketch(context, id + "F6", { "sketchPlane" : qUnion([Q0])});
            skLineSegment(sketch, "E16.0", {"start": v(63.93, 27.37) * mm, "end": v(54.87, 27.37) * mm});
            skLineSegment(sketch, "E16.1", {"start": v(54.87, 27.37) * mm, "end": v(50.35, 35.21) * mm});
            skLineSegment(sketch, "E16.5", {"start": v(68.35, 35.21) * mm, "end": v(63.93, 27.37) * mm});
            skLineSegment(sketch, "E17", {"start": v(68.35, 35.21) * mm, "end": v(50.35, 35.21) * mm});
            skCircle(sketch, "E18", {"center": v(59.54, 31.74) * mm, "radius": 1.5 * mm});
            skSolve(sketch);
        }
        {
            var Q0;
            Q0=makeQuery(id+"F6.imprint","IMPRINT",FACE,{"disambiguationData":[TD([[makeQuery(id+"F6.imprint","IMPRINT",EDGE,{"derivedFrom":sQuery(id+"F6.wireOp",EDGE,"E16.0")}),-1.0]])]});
            extrude(context, id + "F7", {"entities" : qUnion([Q0]), "operationType" : NewBodyOperationType.ADD, "oppositeDirection" : true, "depth" : 2 * mm});
        }
        {
            var Q0;
            Q0=makeQuery(id+"F7.boolean.opBoolean","MERGE",FACE,{"derivedFrom":[makeQuery(id+"F3.opExtrude","CAP_FACE",FACE,{"disambiguationData":[OSD([sQuery(id+"F2.wireOp",EDGE,"E12.bottom"),sQuery(id+"F2.wireOp",EDGE,"E12.top"),sQuery(id+"F2.wireOp",EDGE,"E12.left"),sQuery(id+"F2.wireOp",EDGE,"E12.right")])],"isStart":false}),makeQuery(id+"F7.opExtrude","CAP_FACE",FACE,{"disambiguationData":[OSD([sQuery(id+"F6.wireOp",EDGE,"E16.0"),sQuery(id+"F6.wireOp",EDGE,"E16.1"),sQuery(id+"F6.wireOp",EDGE,"E16.5"),sQuery(id+"F6.wireOp",EDGE,"E17"),sQuery(id+"F6.wireOp",EDGE,"E18")])],"isStart":false})]});
            var sketch = newSketch(context, id + "F8", { "sketchPlane" : qUnion([Q0])});
            skArc(sketch, "E19", {"start": v(-73.77, 34.91) * mm, "mid": v(-77.38, 39.43) * mm, "end": v(-81, 34.91) * mm});
            skSolve(sketch);
        }
        {
            var Q0;
            {var subQ0=sQuery(id+"F8.wireOp",EDGE,"E19");Q0=makeQuery(id+"F8.imprint","IMPRINT",FACE,{"disambiguationData":[TD([[makeQuery(id+"F8.imprint","IMPRINT",EDGE,{"derivedFrom":subQ0}),1.0]])]});}
            var Q1;
            Q1=sQuery(id+"F8.wireOp",EDGE,"E19");
            extrude(context, id + "F9", {"entities" : qUnion([Q0]), "operationType" : NewBodyOperationType.REMOVE, "surfaceEntities" : qUnion([Q1]), "oppositeDirection" : true, "depth" : 2 * mm});
        }
    });
